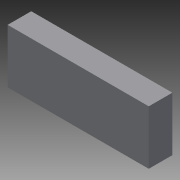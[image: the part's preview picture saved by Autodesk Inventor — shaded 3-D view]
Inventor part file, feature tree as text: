
AUTODESK INVENTOR PART (.ipt)
format: ipt  version: 2013 (Build 170138000, 138)  size: 67,072 bytes
history: native  units: mm
features: extrude x1, sketch x1
ambient origin geometry x8: Origin, YZ Plane, XZ Plane, XY Plane, X Axis, Y Axis, Z Axis, Center Point
bodies: Solid1 (feature_tree)
feature tree (2):
  extrude  "Extrusion1"  Depth=13.3mm
  sketch  "Sketch1"  dims[d0=34.7mm d1=13.3mm d2=5.8mm d3=0.0mm]
